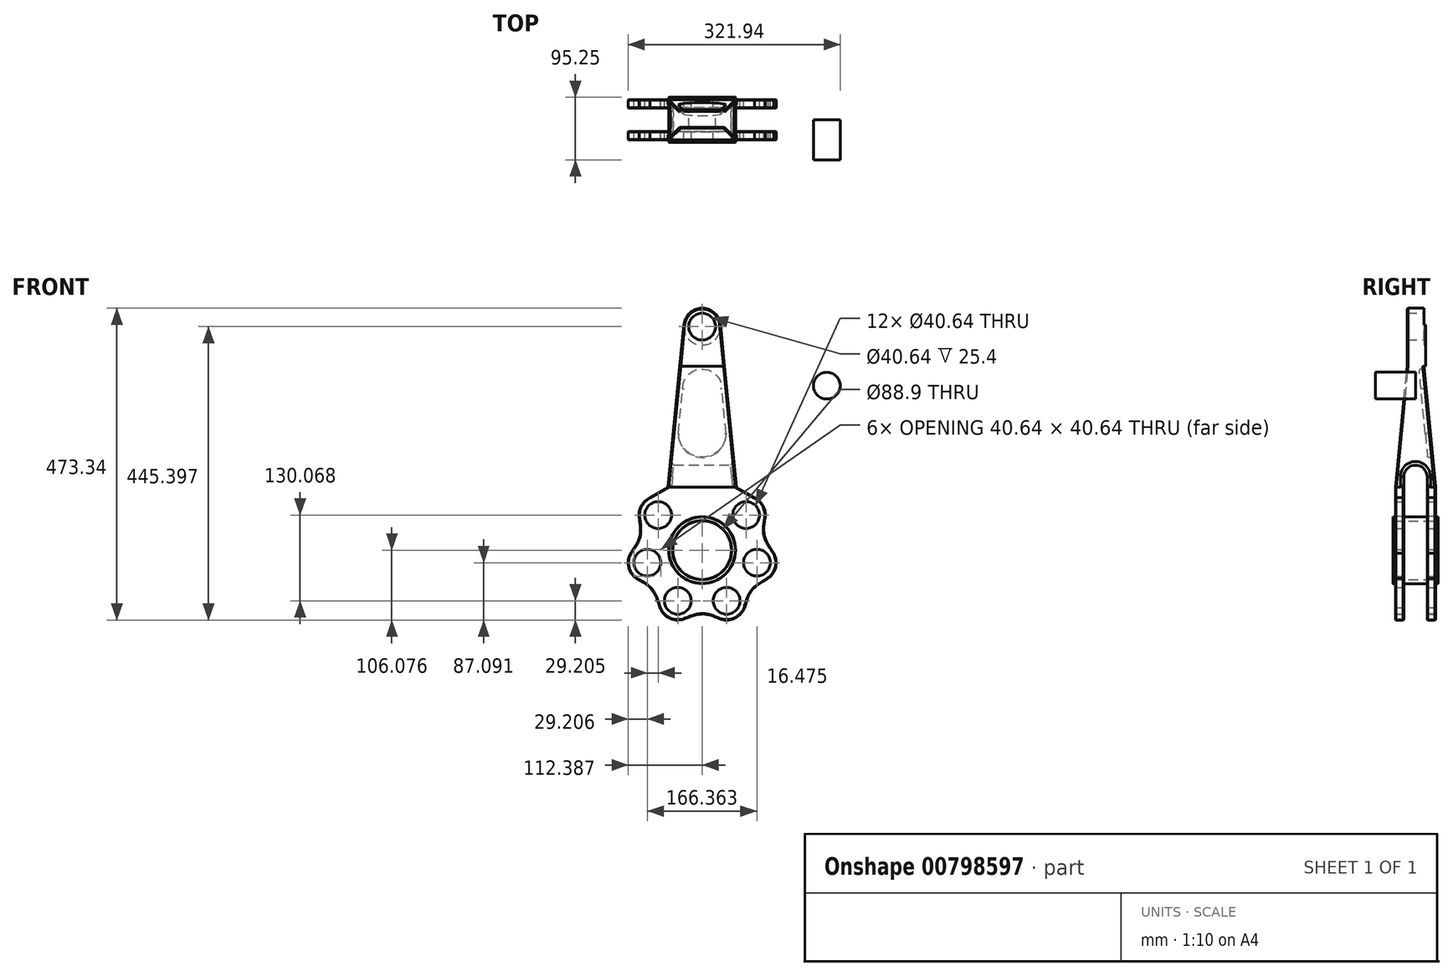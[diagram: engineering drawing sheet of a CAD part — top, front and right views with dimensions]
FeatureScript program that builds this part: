
annotation { "Feature Type Name" : "Feature", "Feature Type Description" : "" }
export const myFeature = defineFeature(function(context is Context, id is Id, definition is map)
    precondition{}
    {
        {
            var Q0;
            Q0=qCreatedBy(makeId("Front.planeOp"),FACE);
            var sketch = newSketch(context, id + "F0", { "sketchPlane" : qUnion([Q0])});
            skCircle(sketch, "E0.cCircle", {"center": v(-40.9, 21.7) * mm, "radius": 76.87 * mm, "construction": true});
            skLineSegment(sketch, "E0.0", {"start": v(-107.6, 74.9) * mm, "end": v(-40.9, 107.03) * mm, "construction": true});
            skLineSegment(sketch, "E0.1", {"start": v(-40.9, 107.03) * mm, "end": v(25.8, 74.9) * mm, "construction": true});
            skLineSegment(sketch, "E0.2", {"start": v(25.8, 74.9) * mm, "end": v(42.28, 2.72) * mm, "construction": true});
            skLineSegment(sketch, "E0.3", {"start": v(42.28, 2.72) * mm, "end": v(-3.88, -55.16) * mm, "construction": true});
            skLineSegment(sketch, "E0.4", {"start": v(-3.88, -55.16) * mm, "end": v(-77.92, -55.16) * mm, "construction": true});
            skLineSegment(sketch, "E0.5", {"start": v(-77.92, -55.16) * mm, "end": v(-124.08, 2.72) * mm, "construction": true});
            skLineSegment(sketch, "E0.6", {"start": v(-124.08, 2.72) * mm, "end": v(-107.6, 74.9) * mm, "construction": true});
            skPoint(sketch, "E0.0.midPoint", {"position": v(-73.39, 91.38) * mm});
            skCircle(sketch, "E1", {"center": v(-107.6, 74.9) * mm, "radius": 20.32 * mm});
            skCircle(sketch, "E2.1.0", {"center": v(-124.08, 2.72) * mm, "radius": 20.32 * mm});
            skCircle(sketch, "E2.2.0", {"center": v(-77.92, -55.16) * mm, "radius": 20.32 * mm});
            skCircle(sketch, "E2.3.0", {"center": v(-3.88, -55.16) * mm, "radius": 20.32 * mm});
            skCircle(sketch, "E2.4.0", {"center": v(42.28, 2.72) * mm, "radius": 20.32 * mm});
            skCircle(sketch, "E2.5.0", {"center": v(25.8, 74.9) * mm, "radius": 20.32 * mm});
            skArc(sketch, "E2.6.0", {"start": v(-59.21, 98.21) * mm, "mid": v(-58.79, 97.38) * mm, "end": v(-58.33, 96.58) * mm});
            skLineSegment(sketch, "E3", {"start": v(-40.9, 21.7) * mm, "end": v(-40.9, 107.03) * mm, "construction": true});
            skLineSegment(sketch, "E4", {"start": v(-40.9, 107.03) * mm, "end": v(-40.9, 361.03) * mm, "construction": true});
            skCircle(sketch, "E5", {"center": v(-107.6, 74.9) * mm, "radius": 29.21 * mm});
            skCircle(sketch, "E6.1.0", {"center": v(-124.08, 2.72) * mm, "radius": 29.21 * mm});
            skCircle(sketch, "E6.2.0", {"center": v(-77.92, -55.16) * mm, "radius": 29.21 * mm});
            skCircle(sketch, "E6.3.0", {"center": v(-3.88, -55.16) * mm, "radius": 29.21 * mm});
            skCircle(sketch, "E6.4.0", {"center": v(42.28, 2.72) * mm, "radius": 29.21 * mm});
            skCircle(sketch, "E6.5.0", {"center": v(25.8, 74.9) * mm, "radius": 29.21 * mm});
            skArc(sketch, "E6.6.0", {"start": v(-67.22, 94.35) * mm, "mid": v(-67.13, 94.17) * mm, "end": v(-67.04, 94) * mm});
            skCircle(sketch, "E7", {"center": v(-40.9, 361.03) * mm, "radius": 20.32 * mm});
            skLineSegment(sketch, "E8", {"start": v(-107.6, 74.9) * mm, "end": v(-120.28, 101.22) * mm, "construction": true});
            skPoint(sketch, "E9", {"position": v(-120.28, 101.22) * mm});
            skPoint(sketch, "E10", {"position": v(-79.92, 105.15) * mm});
            skLineSegment(sketch, "E11", {"start": v(-73.39, 91.38) * mm, "end": v(-69, 81.95) * mm, "construction": true});
            skPoint(sketch, "E12.orphan", {"position": v(-97.62, 102.35) * mm});
            skPoint(sketch, "E13.orphan", {"position": v(-38.78, 107) * mm});
            skArc(sketch, "E14.trimOffspring", {"start": v(-23.48, 96.58) * mm, "mid": v(-23.02, 97.38) * mm, "end": v(-22.6, 98.21) * mm});
            skArc(sketch, "E15.trimOffspring", {"start": v(-14.76, 94) * mm, "mid": v(-14.67, 94.17) * mm, "end": v(-14.59, 94.35) * mm});
            skLineSegment(sketch, "E16", {"start": v(-107.6, 74.9) * mm, "end": v(-40.9, 21.7) * mm, "construction": true});
            skFitSpline(sketch, "E17.MirrorCS", {"points": [v(-136.74, 72.76) * mm, v(-135.47, 43.29) * mm, v(-147.81, 19.76) * mm], "startDerivative": vector(8.77, -57.75) * mm, "endDerivative": vector(-35.1, -48.19) * mm});
            skLineSegment(sketch, "E18", {"start": v(-124.08, 2.72) * mm, "end": v(-40.9, 21.7) * mm, "construction": true});
            skLineSegment(sketch, "E19", {"start": v(-40.9, 21.7) * mm, "end": v(-77.92, -55.16) * mm, "construction": true});
            skLineSegment(sketch, "E20", {"start": v(-40.9, 21.7) * mm, "end": v(-3.88, -55.16) * mm, "construction": true});
            skLineSegment(sketch, "E21", {"start": v(-40.9, 21.7) * mm, "end": v(42.28, 2.72) * mm, "construction": true});
            skLineSegment(sketch, "E22", {"start": v(-40.9, 21.7) * mm, "end": v(25.8, 74.9) * mm, "construction": true});
            skFitSpline(sketch, "E23.MirrorCS", {"points": [v(-105.1, -65.87) * mm, v(-116.74, -38.77) * mm, v(-138.07, -22.92) * mm], "startDerivative": vector(-17.15, 55.83) * mm, "endDerivative": vector(-52.53, 28.19) * mm});
            skFitSpline(sketch, "E24.MirrorCS", {"points": [v(-69.35, -83.09) * mm, v(-40.9, -75.29) * mm, v(-15.21, -82.09) * mm], "startDerivative": vector(54.35, 21.4) * mm, "endDerivative": vector(54.79, -23.5) * mm});
            skFitSpline(sketch, "E25.MirrorCS", {"points": [v(58.77, -21.4) * mm, v(34.93, -38.77) * mm, v(24.23, -63.1) * mm], "startDerivative": vector(-50.62, -29.14) * mm, "endDerivative": vector(-15.8, -57.48) * mm});
            skFitSpline(sketch, "E26.MirrorCS", {"points": [v(67.6, 17.3) * mm, v(53.66, 43.29) * mm, v(54.57, 69.85) * mm], "startDerivative": vector(-32.96, 48.22) * mm, "endDerivative": vector(10.71, 58.64) * mm});
            skLineSegment(sketch, "E27", {"start": v(-120.28, 101.22) * mm, "end": v(-92.79, 117.19) * mm});
            skCircle(sketch, "E28", {"center": v(-40.9, 361.03) * mm, "radius": 27.94 * mm});
            skLineSegment(sketch, "E29", {"start": v(-92.79, 117.19) * mm, "end": v(-68.71, 363.74) * mm});
            skLineSegment(sketch, "E30.MirrorCS", {"start": v(10.98, 117.19) * mm, "end": v(-13.1, 363.74) * mm});
            skLineSegment(sketch, "E31.MirrorCS", {"start": v(38.48, 101.22) * mm, "end": v(10.98, 117.19) * mm});
            skLineSegment(sketch, "E32.0", {"start": v(-40.9, 21.7) * mm, "end": v(-73.39, 91.38) * mm, "construction": true});
            skLineSegment(sketch, "E33", {"start": v(-40.9, 21.7) * mm, "end": v(63.74, 45.6) * mm, "construction": true});
            skLineSegment(sketch, "E34", {"start": v(-107.6, 74.9) * mm, "end": v(67.22, -64.52) * mm, "construction": true});
            skLineSegment(sketch, "E35", {"start": v(42.28, 2.72) * mm, "end": v(-220.12, 62.61) * mm, "construction": true});
            skCircle(sketch, "E36", {"center": v(-40.9, 21.7) * mm, "radius": 50.8 * mm});
            skCircle(sketch, "E37", {"center": v(-40.9, 21.7) * mm, "radius": 44.45 * mm});
            skLineSegment(sketch, "E38", {"start": v(-92.79, 117.19) * mm, "end": v(10.98, 117.19) * mm, "construction": true});
            skSolve(sketch);
        }
        {
            var Q0;
            {var subQ20=sQuery(id+"F0.wireOp",EDGE,"E27");Q0=makeQuery(id+"F0.imprint","IMPRINT",FACE,{"disambiguationData":[TD([[makeQuery(id+"F0.imprint","IMPRINT",EDGE,{"derivedFrom":subQ20}),-1.0]])]});}
            var Q1;
            Q1=makeQuery(id+"F0.imprint","IMPRINT",FACE,{"disambiguationData":[TD([[makeQuery(id+"F0.imprint","IMPRINT",EDGE,{"derivedFrom":sQuery(id+"F0.wireOp",EDGE,"E2.5.0")}),-1.0]])]});
            var Q2;
            Q2=makeQuery(id+"F0.imprint","IMPRINT",FACE,{"disambiguationData":[TD([[makeQuery(id+"F0.imprint","IMPRINT",EDGE,{"derivedFrom":sQuery(id+"F0.wireOp",EDGE,"E2.4.0")}),-1.0]])]});
            var Q3;
            Q3=makeQuery(id+"F0.imprint","IMPRINT",FACE,{"disambiguationData":[TD([[makeQuery(id+"F0.imprint","IMPRINT",EDGE,{"derivedFrom":sQuery(id+"F0.wireOp",EDGE,"E2.3.0")}),-1.0]])]});
            var Q4;
            Q4=makeQuery(id+"F0.imprint","IMPRINT",FACE,{"disambiguationData":[TD([[makeQuery(id+"F0.imprint","IMPRINT",EDGE,{"derivedFrom":sQuery(id+"F0.wireOp",EDGE,"E2.2.0")}),-1.0]])]});
            var Q5;
            Q5=makeQuery(id+"F0.imprint","IMPRINT",FACE,{"disambiguationData":[TD([[makeQuery(id+"F0.imprint","IMPRINT",EDGE,{"derivedFrom":sQuery(id+"F0.wireOp",EDGE,"E2.1.0")}),-1.0]])]});
            var Q6;
            Q6=makeQuery(id+"F0.imprint","IMPRINT",FACE,{"disambiguationData":[TD([[makeQuery(id+"F0.imprint","IMPRINT",EDGE,{"derivedFrom":sQuery(id+"F0.wireOp",EDGE,"E1")}),-1.0]])]});
            var Q7;
            Q7=makeQuery(id+"F0.imprint","IMPRINT",FACE,{"disambiguationData":[TD([[makeQuery(id+"F0.imprint","IMPRINT",EDGE,{"derivedFrom":sQuery(id+"F0.wireOp",EDGE,"E7")}),-1.0]])]});
            extrude(context, id + "F1", {"entities" : qUnion([Q0, Q1, Q2, Q3, Q4, Q5, Q6, Q7]), "endBound" : BoundingType.SYMMETRIC, "depth" : 60.96 * mm});
        }
        {
            var Q0;
            Q0=qCreatedBy(makeId("Right.planeOp"),FACE);
            var sketch = newSketch(context, id + "F2", { "sketchPlane" : qUnion([Q0])});
            skLineSegment(sketch, "E39", {"start": v(-17.78, -123.4) * mm, "end": v(-17.78, 132.94) * mm});
            skLineSegment(sketch, "E40", {"start": v(0, 0) * mm, "end": v(0, 25.84) * mm, "construction": true});
            skLineSegment(sketch, "E41.MirrorCS", {"start": v(17.78, -123.4) * mm, "end": v(17.78, 132.94) * mm});
            skArc(sketch, "E42", {"start": v(-17.78, 132.94) * mm, "mid": v(0, 150.72) * mm, "end": v(17.78, 132.94) * mm});
            skLineSegment(sketch, "E43", {"start": v(-17.78, -123.4) * mm, "end": v(17.78, -123.4) * mm});
            skSolve(sketch);
        }
        {
            var Q0;
            {var subQ0=sQuery(id+"F2.wireOp",EDGE,"E42");Q0=makeQuery(id+"F2.imprint","IMPRINT",FACE,{"disambiguationData":[TD([[makeQuery(id+"F2.imprint","IMPRINT",EDGE,{"derivedFrom":subQ0}),-1.0]])]});}
            var Q1;
            {var subQ0=sQuery(id+"F2.wireOp",EDGE,"E39");Q1=makeQuery(id+"F2.imprint","IMPRINT",FACE,{"disambiguationData":[TD([[makeQuery(id+"F2.imprint","IMPRINT",EDGE,{"derivedFrom":subQ0}),-1.0]])]});}
            extrude(context, id + "F3", {"entities" : qUnion([Q0, Q1]), "operationType" : NewBodyOperationType.REMOVE, "endBound" : BoundingType.SYMMETRIC, "oppositeDirection" : true, "depth" : 382.02 * mm});
        }
        {
            var Q0;
            Q0=qCreatedBy(makeId("Right.planeOp"),FACE);
            var sketch = newSketch(context, id + "F4", { "sketchPlane" : qUnion([Q0])});
            skLineSegment(sketch, "E44", {"start": v(0, 389.03) * mm, "end": v(12.7, 389.03) * mm});
            skLineSegment(sketch, "E45", {"start": v(12.7, 389.03) * mm, "end": v(12.7, 300.73) * mm});
            skLineSegment(sketch, "E46", {"start": v(12.7, 300.73) * mm, "end": v(30.48, 117.19) * mm});
            skLineSegment(sketch, "E47", {"start": v(30.48, 117.19) * mm, "end": v(68.65, 120.89) * mm});
            skLineSegment(sketch, "E48", {"start": v(68.65, 120.89) * mm, "end": v(77.77, 388.8) * mm});
            skLineSegment(sketch, "E49", {"start": v(77.77, 388.8) * mm, "end": v(12.7, 389.03) * mm});
            skLineSegment(sketch, "E50.MirrorCS", {"start": v(-12.7, 300.73) * mm, "end": v(-30.48, 117.19) * mm});
            skLineSegment(sketch, "E51.MirrorCS", {"start": v(-12.7, 389.03) * mm, "end": v(-12.7, 300.73) * mm});
            skLineSegment(sketch, "E52.MirrorCS", {"start": v(-30.48, 117.19) * mm, "end": v(-68.65, 120.89) * mm});
            skLineSegment(sketch, "E53.MirrorCS", {"start": v(-68.65, 120.89) * mm, "end": v(-77.77, 388.8) * mm});
            skLineSegment(sketch, "E54.MirrorCS", {"start": v(-77.77, 388.8) * mm, "end": v(-12.7, 389.03) * mm});
            skPoint(sketch, "E55", {"position": v(25.42, 117.19) * mm});
            skSolve(sketch);
        }
        {
            var Q0;
            Q0=makeQuery(id+"F4.imprint","IMPRINT",FACE,{"disambiguationData":[TD([[makeQuery(id+"F4.imprint","IMPRINT",EDGE,{"derivedFrom":sQuery(id+"F4.wireOp",EDGE,"E45")}),1.0]])]});
            var Q1;
            Q1=makeQuery(id+"F4.imprint","IMPRINT",FACE,{"disambiguationData":[TD([[makeQuery(id+"F4.imprint","IMPRINT",EDGE,{"derivedFrom":sQuery(id+"F4.wireOp",EDGE,"E50.MirrorCS")}),-1.0]])]});
            extrude(context, id + "F5", {"entities" : qUnion([Q0, Q1]), "operationType" : NewBodyOperationType.REMOVE, "endBound" : BoundingType.SYMMETRIC, "oppositeDirection" : true, "depth" : 528.32 * mm});
        }
        {
            var Q0;
            Q0=qCreatedBy(makeId("Front.planeOp"),FACE);
            var sketch = newSketch(context, id + "F6", { "sketchPlane" : qUnion([Q0])});
            skCircle(sketch, "E56", {"center": v(148.33, 271.36) * mm, "radius": 20.32 * mm});
            skSolve(sketch);
        }
        {
            var Q0;
            Q0=makeQuery(id+"F6.imprint","IMPRINT",FACE,{"disambiguationData":[TD([[makeQuery(id+"F6.imprint","IMPRINT",EDGE,{"derivedFrom":sQuery(id+"F6.wireOp",EDGE,"E56")}),1.0]])]});
            extrude(context, id + "F7", {"entities" : qUnion([Q0]), "depth" : 60.96 * mm});
        }
        {
            var Q0;
            Q0=makeQuery(id+"F1.opExtrude","CAP_EDGE",EDGE,{"disambiguationData":[OSD([sQuery(id+"F0.wireOp",EDGE,"E26.MirrorCS")])],"isStart":false});
            var Q1;
            Q1=makeQuery(id+"F1.opExtrude","CAP_EDGE",EDGE,{"disambiguationData":[OSD([sQuery(id+"F0.wireOp",EDGE,"E6.4.0")])],"isStart":false});
            var Q2;
            Q2=makeQuery(id+"F1.opExtrude","CAP_EDGE",EDGE,{"disambiguationData":[OSD([sQuery(id+"F0.wireOp",EDGE,"E25.MirrorCS")])],"isStart":false});
            var Q3;
            Q3=makeQuery(id+"F1.opExtrude","CAP_EDGE",EDGE,{"disambiguationData":[OSD([sQuery(id+"F0.wireOp",EDGE,"E24.MirrorCS")])],"isStart":false});
            var Q4;
            Q4=makeQuery(id+"F1.opExtrude","CAP_EDGE",EDGE,{"disambiguationData":[OSD([sQuery(id+"F0.wireOp",EDGE,"E6.3.0")])],"isStart":false});
            var Q5;
            Q5=makeQuery(id+"F1.opExtrude","CAP_EDGE",EDGE,{"disambiguationData":[OSD([sQuery(id+"F0.wireOp",EDGE,"E6.2.0")])],"isStart":false});
            var Q6;
            Q6=makeQuery(id+"F1.opExtrude","CAP_EDGE",EDGE,{"disambiguationData":[OSD([sQuery(id+"F0.wireOp",EDGE,"E23.MirrorCS")])],"isStart":false});
            var Q7;
            Q7=makeQuery(id+"F1.opExtrude","CAP_EDGE",EDGE,{"disambiguationData":[OSD([sQuery(id+"F0.wireOp",EDGE,"E6.1.0")])],"isStart":false});
            var Q8;
            Q8=makeQuery(id+"F1.opExtrude","CAP_EDGE",EDGE,{"disambiguationData":[OSD([sQuery(id+"F0.wireOp",EDGE,"E17.MirrorCS")])],"isStart":false});
            var Q9;
            Q9=makeQuery(id+"F1.opExtrude","CAP_EDGE",EDGE,{"disambiguationData":[OSD([sQuery(id+"F0.wireOp",EDGE,"E5")])],"isStart":false});
            var Q10;
            Q10=makeQuery(id+"F1.opExtrude","CAP_EDGE",EDGE,{"disambiguationData":[OSD([sQuery(id+"F0.wireOp",EDGE,"E27")])],"isStart":false});
            var Q11;
            Q11=makeQuery(id+"F1.opExtrude","CAP_EDGE",EDGE,{"disambiguationData":[OSD([sQuery(id+"F0.wireOp",EDGE,"E31.MirrorCS")])],"isStart":false});
            var Q12;
            Q12=makeQuery(id+"F1.opExtrude","CAP_EDGE",EDGE,{"disambiguationData":[OSD([sQuery(id+"F0.wireOp",EDGE,"E6.5.0")])],"isStart":false});
            var Q13;
            Q13=makeQuery(id+"F1.opExtrude","CAP_EDGE",EDGE,{"disambiguationData":[OSD([sQuery(id+"F0.wireOp",EDGE,"E27")])],"isStart":true});
            var Q14;
            Q14=makeQuery(id+"F1.opExtrude","CAP_EDGE",EDGE,{"disambiguationData":[OSD([sQuery(id+"F0.wireOp",EDGE,"E5")])],"isStart":true});
            var Q15;
            Q15=makeQuery(id+"F1.opExtrude","CAP_EDGE",EDGE,{"disambiguationData":[OSD([sQuery(id+"F0.wireOp",EDGE,"E17.MirrorCS")])],"isStart":true});
            var Q16;
            Q16=makeQuery(id+"F1.opExtrude","CAP_EDGE",EDGE,{"disambiguationData":[OSD([sQuery(id+"F0.wireOp",EDGE,"E6.1.0")])],"isStart":true});
            var Q17;
            Q17=makeQuery(id+"F1.opExtrude","CAP_EDGE",EDGE,{"disambiguationData":[OSD([sQuery(id+"F0.wireOp",EDGE,"E23.MirrorCS")])],"isStart":true});
            var Q18;
            Q18=makeQuery(id+"F1.opExtrude","CAP_EDGE",EDGE,{"disambiguationData":[OSD([sQuery(id+"F0.wireOp",EDGE,"E6.2.0")])],"isStart":true});
            var Q19;
            Q19=makeQuery(id+"F1.opExtrude","CAP_EDGE",EDGE,{"disambiguationData":[OSD([sQuery(id+"F0.wireOp",EDGE,"E24.MirrorCS")])],"isStart":true});
            var Q20;
            Q20=makeQuery(id+"F1.opExtrude","CAP_EDGE",EDGE,{"disambiguationData":[OSD([sQuery(id+"F0.wireOp",EDGE,"E6.3.0")])],"isStart":true});
            var Q21;
            Q21=makeQuery(id+"F1.opExtrude","CAP_EDGE",EDGE,{"disambiguationData":[OSD([sQuery(id+"F0.wireOp",EDGE,"E25.MirrorCS")])],"isStart":true});
            var Q22;
            Q22=makeQuery(id+"F1.opExtrude","CAP_EDGE",EDGE,{"disambiguationData":[OSD([sQuery(id+"F0.wireOp",EDGE,"E6.4.0")])],"isStart":true});
            var Q23;
            Q23=makeQuery(id+"F1.opExtrude","CAP_EDGE",EDGE,{"disambiguationData":[OSD([sQuery(id+"F0.wireOp",EDGE,"E26.MirrorCS")])],"isStart":true});
            var Q24;
            Q24=makeQuery(id+"F1.opExtrude","CAP_EDGE",EDGE,{"disambiguationData":[OSD([sQuery(id+"F0.wireOp",EDGE,"E6.5.0")])],"isStart":true});
            var Q25;
            Q25=makeQuery(id+"F1.opExtrude","CAP_EDGE",EDGE,{"disambiguationData":[OSD([sQuery(id+"F0.wireOp",EDGE,"E31.MirrorCS")])],"isStart":true});
            chamfer(context, id + "F8", {"entities" : qUnion([Q0, Q1, Q2, Q3, Q4, Q5, Q6, Q7, Q8, Q9, Q10, Q11, Q12, Q13, Q14, Q15, Q16, Q17, Q18, Q19, Q20, Q21, Q22, Q23, Q24, Q25]), "width" : 0.76 * mm, "tangentPropagation" : true});
        }
        {
            var Q0;
            Q0=makeQuery(id+"F3.boolean.opBoolean","INTERSECT",EDGE,{"derivedFrom":[makeQuery(id+"F1.opExtrude","SWEPT_FACE",FACE,{"disambiguationData":[OSD([sQuery(id+"F0.wireOp",EDGE,"E30.MirrorCS")])]}),makeQuery(id+"F3.opExtrude","SWEPT_FACE",FACE,{"disambiguationData":[OSD([sQuery(id+"F2.wireOp",EDGE,"E42")])]})]});
            var Q1;
            Q1=makeQuery(id+"F3.boolean.opBoolean","INTERSECT",EDGE,{"derivedFrom":[makeQuery(id+"F1.opExtrude","SWEPT_FACE",FACE,{"disambiguationData":[OSD([sQuery(id+"F0.wireOp",EDGE,"E29")])]}),makeQuery(id+"F3.opExtrude","SWEPT_FACE",FACE,{"disambiguationData":[OSD([sQuery(id+"F2.wireOp",EDGE,"E42")])]})]});
            chamfer(context, id + "F9", {"entities" : qUnion([Q0, Q1]), "width" : 5.08 * mm, "tangentPropagation" : true});
        }
        {
            var Q0;
            Q0=makeQuery(id+"F3.boolean.opBoolean","INTERSECT",EDGE,{"derivedFrom":[makeQuery(id+"F1.opExtrude","SWEPT_FACE",FACE,{"disambiguationData":[OSD([sQuery(id+"F0.wireOp",EDGE,"E27")])]}),makeQuery(id+"F3.opExtrude","SWEPT_FACE",FACE,{"disambiguationData":[OSD([sQuery(id+"F2.wireOp",EDGE,"E41.MirrorCS")])]})]});
            var Q1;
            Q1=makeQuery(id+"F3.boolean.opBoolean","INTERSECT",EDGE,{"derivedFrom":[makeQuery(id+"F1.opExtrude","SWEPT_FACE",FACE,{"disambiguationData":[OSD([sQuery(id+"F0.wireOp",EDGE,"E5")])]}),makeQuery(id+"F3.opExtrude","SWEPT_FACE",FACE,{"disambiguationData":[OSD([sQuery(id+"F2.wireOp",EDGE,"E41.MirrorCS")])]})]});
            var Q2;
            Q2=makeQuery(id+"F3.boolean.opBoolean","INTERSECT",EDGE,{"derivedFrom":[makeQuery(id+"F1.opExtrude","SWEPT_FACE",FACE,{"disambiguationData":[OSD([sQuery(id+"F0.wireOp",EDGE,"E17.MirrorCS")])]}),makeQuery(id+"F3.opExtrude","SWEPT_FACE",FACE,{"disambiguationData":[OSD([sQuery(id+"F2.wireOp",EDGE,"E41.MirrorCS")])]})]});
            var Q3;
            Q3=makeQuery(id+"F3.boolean.opBoolean","INTERSECT",EDGE,{"derivedFrom":[makeQuery(id+"F1.opExtrude","SWEPT_FACE",FACE,{"disambiguationData":[OSD([sQuery(id+"F0.wireOp",EDGE,"E6.1.0")])]}),makeQuery(id+"F3.opExtrude","SWEPT_FACE",FACE,{"disambiguationData":[OSD([sQuery(id+"F2.wireOp",EDGE,"E41.MirrorCS")])]})]});
            var Q4;
            Q4=makeQuery(id+"F3.boolean.opBoolean","INTERSECT",EDGE,{"derivedFrom":[makeQuery(id+"F1.opExtrude","SWEPT_FACE",FACE,{"disambiguationData":[OSD([sQuery(id+"F0.wireOp",EDGE,"E23.MirrorCS")])]}),makeQuery(id+"F3.opExtrude","SWEPT_FACE",FACE,{"disambiguationData":[OSD([sQuery(id+"F2.wireOp",EDGE,"E41.MirrorCS")])]})]});
            var Q5;
            Q5=makeQuery(id+"F3.boolean.opBoolean","INTERSECT",EDGE,{"derivedFrom":[makeQuery(id+"F1.opExtrude","SWEPT_FACE",FACE,{"disambiguationData":[OSD([sQuery(id+"F0.wireOp",EDGE,"E6.2.0")])]}),makeQuery(id+"F3.opExtrude","SWEPT_FACE",FACE,{"disambiguationData":[OSD([sQuery(id+"F2.wireOp",EDGE,"E41.MirrorCS")])]})]});
            var Q6;
            Q6=makeQuery(id+"F3.boolean.opBoolean","INTERSECT",EDGE,{"derivedFrom":[makeQuery(id+"F1.opExtrude","SWEPT_FACE",FACE,{"disambiguationData":[OSD([sQuery(id+"F0.wireOp",EDGE,"E23.MirrorCS")])]}),makeQuery(id+"F3.opExtrude","SWEPT_FACE",FACE,{"disambiguationData":[OSD([sQuery(id+"F2.wireOp",EDGE,"E39")])]})]});
            var Q7;
            Q7=makeQuery(id+"F3.boolean.opBoolean","INTERSECT",EDGE,{"derivedFrom":[makeQuery(id+"F1.opExtrude","SWEPT_FACE",FACE,{"disambiguationData":[OSD([sQuery(id+"F0.wireOp",EDGE,"E6.1.0")])]}),makeQuery(id+"F3.opExtrude","SWEPT_FACE",FACE,{"disambiguationData":[OSD([sQuery(id+"F2.wireOp",EDGE,"E39")])]})]});
            var Q8;
            Q8=makeQuery(id+"F3.boolean.opBoolean","INTERSECT",EDGE,{"derivedFrom":[makeQuery(id+"F1.opExtrude","SWEPT_FACE",FACE,{"disambiguationData":[OSD([sQuery(id+"F0.wireOp",EDGE,"E17.MirrorCS")])]}),makeQuery(id+"F3.opExtrude","SWEPT_FACE",FACE,{"disambiguationData":[OSD([sQuery(id+"F2.wireOp",EDGE,"E39")])]})]});
            var Q9;
            Q9=makeQuery(id+"F3.boolean.opBoolean","INTERSECT",EDGE,{"derivedFrom":[makeQuery(id+"F1.opExtrude","SWEPT_FACE",FACE,{"disambiguationData":[OSD([sQuery(id+"F0.wireOp",EDGE,"E5")])]}),makeQuery(id+"F3.opExtrude","SWEPT_FACE",FACE,{"disambiguationData":[OSD([sQuery(id+"F2.wireOp",EDGE,"E39")])]})]});
            var Q10;
            Q10=makeQuery(id+"F3.boolean.opBoolean","INTERSECT",EDGE,{"derivedFrom":[makeQuery(id+"F1.opExtrude","SWEPT_FACE",FACE,{"disambiguationData":[OSD([sQuery(id+"F0.wireOp",EDGE,"E27")])]}),makeQuery(id+"F3.opExtrude","SWEPT_FACE",FACE,{"disambiguationData":[OSD([sQuery(id+"F2.wireOp",EDGE,"E39")])]})]});
            var Q11;
            Q11=makeQuery(id+"F3.boolean.opBoolean","INTERSECT",EDGE,{"derivedFrom":[makeQuery(id+"F1.opExtrude","SWEPT_FACE",FACE,{"disambiguationData":[OSD([sQuery(id+"F0.wireOp",EDGE,"E6.2.0")])]}),makeQuery(id+"F3.opExtrude","SWEPT_FACE",FACE,{"disambiguationData":[OSD([sQuery(id+"F2.wireOp",EDGE,"E39")])]})]});
            var Q12;
            Q12=makeQuery(id+"F3.boolean.opBoolean","INTERSECT",EDGE,{"derivedFrom":[makeQuery(id+"F1.opExtrude","SWEPT_FACE",FACE,{"disambiguationData":[OSD([sQuery(id+"F0.wireOp",EDGE,"E24.MirrorCS")])]}),makeQuery(id+"F3.opExtrude","SWEPT_FACE",FACE,{"disambiguationData":[OSD([sQuery(id+"F2.wireOp",EDGE,"E39")])]})]});
            var Q13;
            Q13=makeQuery(id+"F3.boolean.opBoolean","INTERSECT",EDGE,{"derivedFrom":[makeQuery(id+"F1.opExtrude","SWEPT_FACE",FACE,{"disambiguationData":[OSD([sQuery(id+"F0.wireOp",EDGE,"E24.MirrorCS")])]}),makeQuery(id+"F3.opExtrude","SWEPT_FACE",FACE,{"disambiguationData":[OSD([sQuery(id+"F2.wireOp",EDGE,"E41.MirrorCS")])]})]});
            var Q14;
            Q14=makeQuery(id+"F3.boolean.opBoolean","INTERSECT",EDGE,{"derivedFrom":[makeQuery(id+"F1.opExtrude","SWEPT_FACE",FACE,{"disambiguationData":[OSD([sQuery(id+"F0.wireOp",EDGE,"E6.3.0")])]}),makeQuery(id+"F3.opExtrude","SWEPT_FACE",FACE,{"disambiguationData":[OSD([sQuery(id+"F2.wireOp",EDGE,"E39")])]})]});
            var Q15;
            Q15=makeQuery(id+"F3.boolean.opBoolean","INTERSECT",EDGE,{"derivedFrom":[makeQuery(id+"F1.opExtrude","SWEPT_FACE",FACE,{"disambiguationData":[OSD([sQuery(id+"F0.wireOp",EDGE,"E6.3.0")])]}),makeQuery(id+"F3.opExtrude","SWEPT_FACE",FACE,{"disambiguationData":[OSD([sQuery(id+"F2.wireOp",EDGE,"E41.MirrorCS")])]})]});
            var Q16;
            Q16=makeQuery(id+"F3.boolean.opBoolean","INTERSECT",EDGE,{"derivedFrom":[makeQuery(id+"F1.opExtrude","SWEPT_FACE",FACE,{"disambiguationData":[OSD([sQuery(id+"F0.wireOp",EDGE,"E25.MirrorCS")])]}),makeQuery(id+"F3.opExtrude","SWEPT_FACE",FACE,{"disambiguationData":[OSD([sQuery(id+"F2.wireOp",EDGE,"E41.MirrorCS")])]})]});
            var Q17;
            Q17=makeQuery(id+"F3.boolean.opBoolean","INTERSECT",EDGE,{"derivedFrom":[makeQuery(id+"F1.opExtrude","SWEPT_FACE",FACE,{"disambiguationData":[OSD([sQuery(id+"F0.wireOp",EDGE,"E25.MirrorCS")])]}),makeQuery(id+"F3.opExtrude","SWEPT_FACE",FACE,{"disambiguationData":[OSD([sQuery(id+"F2.wireOp",EDGE,"E39")])]})]});
            var Q18;
            Q18=makeQuery(id+"F3.boolean.opBoolean","INTERSECT",EDGE,{"derivedFrom":[makeQuery(id+"F1.opExtrude","SWEPT_FACE",FACE,{"disambiguationData":[OSD([sQuery(id+"F0.wireOp",EDGE,"E26.MirrorCS")])]}),makeQuery(id+"F3.opExtrude","SWEPT_FACE",FACE,{"disambiguationData":[OSD([sQuery(id+"F2.wireOp",EDGE,"E39")])]})]});
            var Q19;
            Q19=makeQuery(id+"F3.boolean.opBoolean","INTERSECT",EDGE,{"derivedFrom":[makeQuery(id+"F1.opExtrude","SWEPT_FACE",FACE,{"disambiguationData":[OSD([sQuery(id+"F0.wireOp",EDGE,"E26.MirrorCS")])]}),makeQuery(id+"F3.opExtrude","SWEPT_FACE",FACE,{"disambiguationData":[OSD([sQuery(id+"F2.wireOp",EDGE,"E41.MirrorCS")])]})]});
            var Q20;
            Q20=makeQuery(id+"F3.boolean.opBoolean","INTERSECT",EDGE,{"derivedFrom":[makeQuery(id+"F1.opExtrude","SWEPT_FACE",FACE,{"disambiguationData":[OSD([sQuery(id+"F0.wireOp",EDGE,"E6.4.0")])]}),makeQuery(id+"F3.opExtrude","SWEPT_FACE",FACE,{"disambiguationData":[OSD([sQuery(id+"F2.wireOp",EDGE,"E41.MirrorCS")])]})]});
            var Q21;
            Q21=makeQuery(id+"F3.boolean.opBoolean","INTERSECT",EDGE,{"derivedFrom":[makeQuery(id+"F1.opExtrude","SWEPT_FACE",FACE,{"disambiguationData":[OSD([sQuery(id+"F0.wireOp",EDGE,"E6.4.0")])]}),makeQuery(id+"F3.opExtrude","SWEPT_FACE",FACE,{"disambiguationData":[OSD([sQuery(id+"F2.wireOp",EDGE,"E39")])]})]});
            var Q22;
            Q22=makeQuery(id+"F3.boolean.opBoolean","INTERSECT",EDGE,{"derivedFrom":[makeQuery(id+"F1.opExtrude","SWEPT_FACE",FACE,{"disambiguationData":[OSD([sQuery(id+"F0.wireOp",EDGE,"E31.MirrorCS")])]}),makeQuery(id+"F3.opExtrude","SWEPT_FACE",FACE,{"disambiguationData":[OSD([sQuery(id+"F2.wireOp",EDGE,"E41.MirrorCS")])]})]});
            var Q23;
            Q23=makeQuery(id+"F3.boolean.opBoolean","INTERSECT",EDGE,{"derivedFrom":[makeQuery(id+"F1.opExtrude","SWEPT_FACE",FACE,{"disambiguationData":[OSD([sQuery(id+"F0.wireOp",EDGE,"E6.5.0")])]}),makeQuery(id+"F3.opExtrude","SWEPT_FACE",FACE,{"disambiguationData":[OSD([sQuery(id+"F2.wireOp",EDGE,"E41.MirrorCS")])]})]});
            var Q24;
            Q24=makeQuery(id+"F3.boolean.opBoolean","INTERSECT",EDGE,{"derivedFrom":[makeQuery(id+"F1.opExtrude","SWEPT_FACE",FACE,{"disambiguationData":[OSD([sQuery(id+"F0.wireOp",EDGE,"E31.MirrorCS")])]}),makeQuery(id+"F3.opExtrude","SWEPT_FACE",FACE,{"disambiguationData":[OSD([sQuery(id+"F2.wireOp",EDGE,"E39")])]})]});
            var Q25;
            Q25=makeQuery(id+"F3.boolean.opBoolean","INTERSECT",EDGE,{"derivedFrom":[makeQuery(id+"F1.opExtrude","SWEPT_FACE",FACE,{"disambiguationData":[OSD([sQuery(id+"F0.wireOp",EDGE,"E6.5.0")])]}),makeQuery(id+"F3.opExtrude","SWEPT_FACE",FACE,{"disambiguationData":[OSD([sQuery(id+"F2.wireOp",EDGE,"E39")])]})]});
            chamfer(context, id + "F10", {"entities" : qUnion([Q0, Q1, Q2, Q3, Q4, Q5, Q6, Q7, Q8, Q9, Q10, Q11, Q12, Q13, Q14, Q15, Q16, Q17, Q18, Q19, Q20, Q21, Q22, Q23, Q24, Q25]), "width" : 0.76 * mm, "tangentPropagation" : true});
        }
        {
            var Q0;
            Q0=makeQuery(id+"F0.imprint","IMPRINT",FACE,{"disambiguationData":[TD([[makeQuery(id+"F0.imprint","IMPRINT",EDGE,{"derivedFrom":sQuery(id+"F0.wireOp",EDGE,"E36")}),1.0]])]});
            extrude(context, id + "F11", {"entities" : qUnion([Q0]), "operationType" : NewBodyOperationType.ADD, "endBound" : BoundingType.SYMMETRIC, "depth" : 68.58 * mm});
        }
        {
            var Q0;
            Q0=makeQuery(id+"F11.opExtrude","CAP_FACE",FACE,{"disambiguationData":[OSD([sQuery(id+"F0.wireOp",EDGE,"E36"),sQuery(id+"F0.wireOp",EDGE,"E37")])],"isStart":true});
            var Q1;
            Q1=makeQuery(id+"F11.opExtrude","CAP_FACE",FACE,{"disambiguationData":[OSD([sQuery(id+"F0.wireOp",EDGE,"E36"),sQuery(id+"F0.wireOp",EDGE,"E37")])],"isStart":false});
            var Q2;
            Q2=makeQuery(id+"F1.opExtrude","CAP_EDGE",EDGE,{"disambiguationData":[OSD([sQuery(id+"F0.wireOp",EDGE,"E36")])],"isStart":false});
            var Q3;
            Q3=makeQuery(id+"F1.opExtrude","CAP_EDGE",EDGE,{"disambiguationData":[OSD([sQuery(id+"F0.wireOp",EDGE,"E36")])],"isStart":true});
            chamfer(context, id + "F12", {"entities" : qUnion([Q0, Q1, Q2, Q3]), "width" : 0.5 * mm, "tangentPropagation" : true});
        }
        {
            var Q0;
            Q0=makeQuery(id+"F5.boolean.opBoolean","COPY",FACE,{"derivedFrom":makeQuery(id+"F5.opExtrude","SWEPT_FACE",FACE,{"disambiguationData":[OSD([sQuery(id+"F4.wireOp",EDGE,"E46")])]})});
            var sketch = newSketch(context, id + "F13", { "sketchPlane" : qUnion([Q0])});
            skLineSegment(sketch, "E57.0", {"start": v(77.15, 195.88) * mm, "end": v(70.47, 264.5) * mm});
            skLineSegment(sketch, "E57.2", {"start": v(4.66, 195.88) * mm, "end": v(11.33, 264.5) * mm});
            skPoint(sketch, "E58", {"position": v(40.9, 358.12) * mm});
            skPoint(sketch, "E59.end.orphan", {"position": v(40.9, 346.54) * mm});
            skPoint(sketch, "E60.orphan", {"position": v(11.33, 264.5) * mm});
            skPoint(sketch, "E61.orphan", {"position": v(70.47, 264.5) * mm});
            skLineSegment(sketch, "E62", {"start": v(4.66, 195.88) * mm, "end": v(77.15, 195.88) * mm, "construction": true});
            skArc(sketch, "E63", {"start": v(4.66, 195.88) * mm, "mid": v(40.9, 159.63) * mm, "end": v(77.15, 195.88) * mm});
            skArc(sketch, "E64", {"start": v(70.47, 264.5) * mm, "mid": v(40.9, 294.07) * mm, "end": v(11.33, 264.5) * mm});
            skLineSegment(sketch, "E65", {"start": v(70.47, 264.5) * mm, "end": v(11.33, 264.5) * mm, "construction": true});
            skSolve(sketch);
        }
        {
            var Q0;
            Q0=makeQuery(id+"F13.imprint","IMPRINT",FACE,{"disambiguationData":[TD([[makeQuery(id+"F13.imprint","IMPRINT",EDGE,{"derivedFrom":sQuery(id+"F13.wireOp",EDGE,"E57.0")}),1.0]])]});
            extrude(context, id + "F14", {"entities" : qUnion([Q0]), "operationType" : NewBodyOperationType.REMOVE, "oppositeDirection" : true, "depth" : 7.62 * mm});
        }
        {
            var Q0;
            Q0=makeQuery(id+"F5.boolean.opBoolean","COPY",FACE,{"derivedFrom":makeQuery(id+"F5.opExtrude","SWEPT_FACE",FACE,{"disambiguationData":[OSD([sQuery(id+"F4.wireOp",EDGE,"E45")])]})});
            var sketch = newSketch(context, id + "F15", { "sketchPlane" : qUnion([Q0])});
            skCircle(sketch, "E66", {"center": v(40.9, 361.03) * mm, "radius": 27.94 * mm});
            skCircle(sketch, "E67", {"center": v(40.9, 361.03) * mm, "radius": 20.32 * mm});
            skSolve(sketch);
        }
        {
            var Q0;
            {var subQ0=sQuery(id+"F15.wireOp",EDGE,"E66");Q0=makeQuery(id+"F15.imprint","IMPRINT",FACE,{"disambiguationData":[TD([[makeQuery(id+"F15.imprint","IMPRINT",EDGE,{"disambiguationData":[OD(0.0)],"derivedFrom":subQ0}),-1.0]])]});}
            extrude(context, id + "F16", {"entities" : qUnion([Q0]), "operationType" : NewBodyOperationType.ADD, "depth" : 2.54 * mm});
        }
        {
            var Q0;
            Q0=makeQuery(id+"F5.boolean.opBoolean","INTERSECT",EDGE,{"derivedFrom":[makeQuery(id+"F1.opExtrude","SWEPT_FACE",FACE,{"disambiguationData":[OSD([sQuery(id+"F0.wireOp",EDGE,"E29")])]}),makeQuery(id+"F5.opExtrude","SWEPT_FACE",FACE,{"disambiguationData":[OSD([sQuery(id+"F4.wireOp",EDGE,"E46")])]})]});
            var Q1;
            Q1=makeQuery(id+"F5.boolean.opBoolean","INTERSECT",EDGE,{"derivedFrom":[makeQuery(id+"F1.opExtrude","SWEPT_FACE",FACE,{"disambiguationData":[OSD([sQuery(id+"F0.wireOp",EDGE,"E29")])]}),makeQuery(id+"F5.opExtrude","SWEPT_FACE",FACE,{"disambiguationData":[OSD([sQuery(id+"F4.wireOp",EDGE,"E45")])]})]});
            var Q2;
            Q2=makeQuery(id+"F5.boolean.opBoolean","INTERSECT",EDGE,{"derivedFrom":[makeQuery(id+"F1.opExtrude","SWEPT_FACE",FACE,{"disambiguationData":[OSD([sQuery(id+"F0.wireOp",EDGE,"E30.MirrorCS")])]}),makeQuery(id+"F5.opExtrude","SWEPT_FACE",FACE,{"disambiguationData":[OSD([sQuery(id+"F4.wireOp",EDGE,"E46")])]})]});
            var Q3;
            Q3=makeQuery(id+"F5.boolean.opBoolean","INTERSECT",EDGE,{"derivedFrom":[makeQuery(id+"F1.opExtrude","SWEPT_FACE",FACE,{"disambiguationData":[OSD([sQuery(id+"F0.wireOp",EDGE,"E30.MirrorCS")])]}),makeQuery(id+"F5.opExtrude","SWEPT_FACE",FACE,{"disambiguationData":[OSD([sQuery(id+"F4.wireOp",EDGE,"E45")])]})]});
            var Q4;
            Q4=makeQuery(id+"F5.boolean.opBoolean","INTERSECT",EDGE,{"derivedFrom":[makeQuery(id+"F1.opExtrude","SWEPT_FACE",FACE,{"disambiguationData":[OSD([sQuery(id+"F0.wireOp",EDGE,"E29")])]}),makeQuery(id+"F5.opExtrude","SWEPT_FACE",FACE,{"disambiguationData":[OSD([sQuery(id+"F4.wireOp",EDGE,"E50.MirrorCS")])]})]});
            var Q5;
            Q5=makeQuery(id+"F5.boolean.opBoolean","INTERSECT",EDGE,{"derivedFrom":[makeQuery(id+"F1.opExtrude","SWEPT_FACE",FACE,{"disambiguationData":[OSD([sQuery(id+"F0.wireOp",EDGE,"E29")])]}),makeQuery(id+"F5.opExtrude","SWEPT_FACE",FACE,{"disambiguationData":[OSD([sQuery(id+"F4.wireOp",EDGE,"E51.MirrorCS")])]})]});
            var Q6;
            Q6=makeQuery(id+"F5.boolean.opBoolean","INTERSECT",EDGE,{"derivedFrom":[makeQuery(id+"F1.opExtrude","SWEPT_FACE",FACE,{"disambiguationData":[OSD([sQuery(id+"F0.wireOp",EDGE,"E30.MirrorCS")])]}),makeQuery(id+"F5.opExtrude","SWEPT_FACE",FACE,{"disambiguationData":[OSD([sQuery(id+"F4.wireOp",EDGE,"E50.MirrorCS")])]})]});
            var Q7;
            Q7=makeQuery(id+"F5.boolean.opBoolean","INTERSECT",EDGE,{"derivedFrom":[makeQuery(id+"F1.opExtrude","SWEPT_FACE",FACE,{"disambiguationData":[OSD([sQuery(id+"F0.wireOp",EDGE,"E30.MirrorCS")])]}),makeQuery(id+"F5.opExtrude","SWEPT_FACE",FACE,{"disambiguationData":[OSD([sQuery(id+"F4.wireOp",EDGE,"E51.MirrorCS")])]})]});
            chamfer(context, id + "F17", {"entities" : qUnion([Q0, Q1, Q2, Q3, Q4, Q5, Q6, Q7]), "width" : 1.4 * mm, "tangentPropagation" : true});
        }
        {
            var Q0;
            Q0=makeQuery(id+"F14.boolean.opBoolean","COPY",FACE,{"derivedFrom":makeQuery(id+"F14.opExtrude","CAP_FACE",FACE,{"disambiguationData":[OSD([sQuery(id+"F13.wireOp",EDGE,"E57.0"),sQuery(id+"F13.wireOp",EDGE,"E57.2"),sQuery(id+"F13.wireOp",EDGE,"E63"),sQuery(id+"F13.wireOp",EDGE,"E64")])],"isStart":false})});
            var Q1;
            Q1=makeQuery(id+"F14.boolean.opBoolean","COPY",EDGE,{"derivedFrom":makeQuery(id+"F14.opExtrude","CAP_EDGE",EDGE,{"disambiguationData":[OSD([sQuery(id+"F13.wireOp",EDGE,"E64")])],"isStart":true})});
            var Q2;
            Q2=makeQuery(id+"F14.boolean.opBoolean","COPY",EDGE,{"derivedFrom":makeQuery(id+"F14.opExtrude","CAP_EDGE",EDGE,{"disambiguationData":[OSD([sQuery(id+"F13.wireOp",EDGE,"E57.2")])],"isStart":true})});
            var Q3;
            Q3=makeQuery(id+"F14.boolean.opBoolean","COPY",EDGE,{"derivedFrom":makeQuery(id+"F14.opExtrude","CAP_EDGE",EDGE,{"disambiguationData":[OSD([sQuery(id+"F13.wireOp",EDGE,"E63")])],"isStart":true})});
            var Q4;
            Q4=makeQuery(id+"F14.boolean.opBoolean","COPY",EDGE,{"derivedFrom":makeQuery(id+"F14.opExtrude","CAP_EDGE",EDGE,{"disambiguationData":[OSD([sQuery(id+"F13.wireOp",EDGE,"E57.0")])],"isStart":true})});
            var Q5;
            Q5=makeQuery(id+"FNEhdAecueqq2wd_2.1.F14.boolean.opBoolean","COPY",FACE,{"derivedFrom":makeQuery(id+"FNEhdAecueqq2wd_2.1.F14.opExtrude","CAP_FACE",FACE,{"disambiguationData":[OSD([sQuery(id+"F13.wireOp",EDGE,"E57.0"),sQuery(id+"F13.wireOp",EDGE,"E57.2"),sQuery(id+"F13.wireOp",EDGE,"E63"),sQuery(id+"F13.wireOp",EDGE,"E64")])],"isStart":false})});
            var Q6;
            Q6=makeQuery(id+"FNEhdAecueqq2wd_2.1.F14.boolean.opBoolean","COPY",EDGE,{"derivedFrom":makeQuery(id+"FNEhdAecueqq2wd_2.1.F14.opExtrude","CAP_EDGE",EDGE,{"disambiguationData":[OSD([sQuery(id+"F13.wireOp",EDGE,"E57.2")])],"isStart":true})});
            var Q7;
            Q7=makeQuery(id+"FNEhdAecueqq2wd_2.1.F14.boolean.opBoolean","COPY",EDGE,{"derivedFrom":makeQuery(id+"FNEhdAecueqq2wd_2.1.F14.opExtrude","CAP_EDGE",EDGE,{"disambiguationData":[OSD([sQuery(id+"F13.wireOp",EDGE,"E64")])],"isStart":true})});
            var Q8;
            Q8=makeQuery(id+"FNEhdAecueqq2wd_2.1.F14.boolean.opBoolean","COPY",EDGE,{"derivedFrom":makeQuery(id+"FNEhdAecueqq2wd_2.1.F14.opExtrude","CAP_EDGE",EDGE,{"disambiguationData":[OSD([sQuery(id+"F13.wireOp",EDGE,"E57.0")])],"isStart":true})});
            var Q9;
            Q9=makeQuery(id+"FNEhdAecueqq2wd_2.1.F14.boolean.opBoolean","COPY",EDGE,{"derivedFrom":makeQuery(id+"FNEhdAecueqq2wd_2.1.F14.opExtrude","CAP_EDGE",EDGE,{"disambiguationData":[OSD([sQuery(id+"F13.wireOp",EDGE,"E63")])],"isStart":true})});
            fillet(context, id + "F18", {"entities" : qUnion([Q0, Q1, Q2, Q3, Q4, Q5, Q6, Q7, Q8, Q9]), "radius" : 2.3 * mm, "tangentPropagation" : true, "allowEdgeOverflow" : false});
        }
    });
